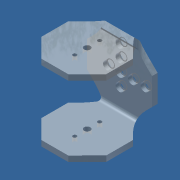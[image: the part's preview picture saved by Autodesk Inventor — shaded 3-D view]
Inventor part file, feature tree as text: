
AUTODESK INVENTOR PART (.ipt)
format: ipt  version: 2014 (Build 180170000, 170)  size: 280,064 bytes
history: native  units: in
note: dims shown in document units (in); Inventor stores cm internally (conversion verified against a paired STEP export)
features: extrude x7, sketch x7, plane x2, fillet x2, mirror x2, projected_geometry x2
ambient origin geometry x8: Origin, YZ Plane, XZ Plane, XY Plane, X Axis, Y Axis, Z Axis, Center Point
bodies: Solid1 (feature_tree)
feature tree (22):
  extrude  "Extrusion1"  TaperAngle=0.0deg  [1 undecoded]
  extrude  "Extrusion2"  Depth=0.1772in
  plane  "Work Plane1"
  extrude  "Extrusion3"  Depth=0.1772in
  fillet  "Fillet1"  [1 undecoded]
  plane  "Work Plane2"
  mirror  "Mirror1"
  fillet  "Fillet2"  Radius=0.1181in
  extrude  "Extrusion4"  Depth=0.5906in
  extrude  "Extrusion5"  Depth=0.1772in
  extrude  "Extrusion6"  Depth=0.2559in
  extrude  "Extrusion7"  Depth=0.3937in
  mirror  "Mirror2"
  sketch  "Sketch1"  dims[d0=2.0472in d3=0.0in]
  sketch  "Sketch2"  dims[d4=2.0472in d5=0.1772in]
  sketch  "Sketch3"  dims[d6=0.0in d7=0.1772in d8=0.0in d9=0.1181in]
  sketch  "Sketch4"  dims[d10=-1.0236in d11=0.5906in]
  sketch  "Sketch5"  dims[d12=0.1969in d15=0.1772in]
  sketch  "Sketch6"  dims[d16=0.0in d17=0.2559in]
  projected_geometry  "Projected Loop1"
  sketch  "Sketch7"  dims[d18=0.2559in d19=0.3937in d20=0.2559in d21=0.3937in d22=0.2559in d23=0.2559in d24=0.3937in d25=0.3937in d26=0.1181in d27=0.0in d28=0.2087in d29=0.2087in d30=0.2087in d31=0.2087in d32=0.2087in d33=0.0197in d34=0.2749in d35=0.1181in d36=0.3937in d37=0.1181in d38=0.3937in d39=0.0in d40=0.0in d41=0.2559in d42=0.2559in d43=0.3937in d44=0.2087in d45=0.2559in d46=0.2559in d47=0.3937in d48=0.2087in]
  projected_geometry  "Projected Loop2"
note: 2 required parameter values undecoded (feature->parameter linkage not recoverable at this tier; creation-order binding heuristic only, values carry confidence <= 0.55)
